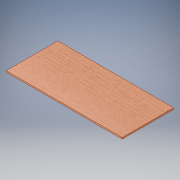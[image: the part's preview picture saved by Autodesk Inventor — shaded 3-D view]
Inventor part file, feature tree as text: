
AUTODESK INVENTOR PART (.ipt)
format: ipt  version: 2017 (Build 210142000, 142)  size: 107,520 bytes
history: native  units: in
note: dims shown in document units (in); Inventor stores cm internally (conversion verified against a paired STEP export)
features: extrude x1, sketch x1
ambient origin geometry x8: Origin, YZ Plane, XZ Plane, XY Plane, X Axis, Y Axis, Z Axis, Center Point
bodies: Solid1 (feature_tree)
feature tree (2):
  extrude  "Extrusion1"  Depth=15.0748in
  sketch  "Sketch1"  dims[d0=6.6929in d1=15.0748in d2=0.1875in d3=0.0in]
